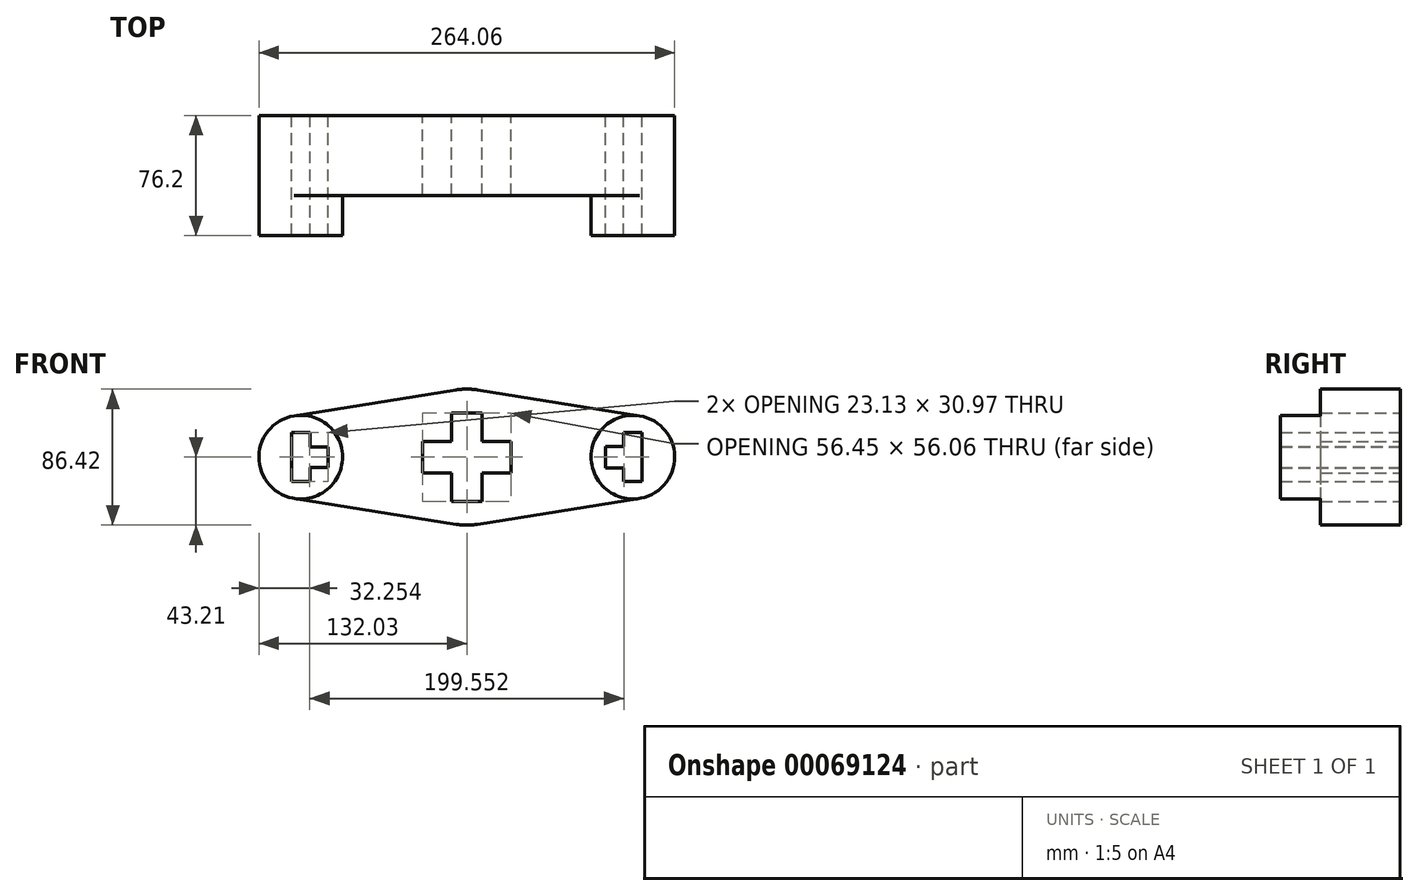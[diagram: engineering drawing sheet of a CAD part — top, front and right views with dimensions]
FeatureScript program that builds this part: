
annotation { "Feature Type Name" : "Feature", "Feature Type Description" : "" }
export const myFeature = defineFeature(function(context is Context, id is Id, definition is map)
    precondition{}
    {
        {
            var Q0;
            Q0=qCreatedBy(makeId("Front.planeOp"),FACE);
            var sketch = newSketch(context, id + "F0", { "sketchPlane" : qUnion([Q0])});
            skCircle(sketch, "E0", {"center": v(0, 0) * mm, "radius": 43.2 * mm});
            skCircle(sketch, "E1", {"center": v(105.46, 0) * mm, "radius": 26.57 * mm});
            skCircle(sketch, "E2", {"center": v(-105.46, 0) * mm, "radius": 26.57 * mm});
            skLineSegment(sketch, "E3", {"start": v(-6.82, 42.66) * mm, "end": v(-109.65, 26.23) * mm});
            skLineSegment(sketch, "E4", {"start": v(-6.82, -42.66) * mm, "end": v(-109.65, -26.23) * mm});
            skLineSegment(sketch, "E5", {"start": v(6.82, 42.66) * mm, "end": v(109.65, 26.23) * mm});
            skLineSegment(sketch, "E6", {"start": v(6.82, -42.66) * mm, "end": v(109.65, -26.23) * mm});
            skLineSegment(sketch, "E7.rect.bottom", {"start": v(-122.71, 6.47) * mm, "end": v(-88.21, 6.47) * mm});
            skLineSegment(sketch, "E7.rect.top", {"start": v(-122.71, -6.47) * mm, "end": v(-88.21, -6.47) * mm});
            skLineSegment(sketch, "E7.rect.left", {"start": v(-122.71, 6.47) * mm, "end": v(-122.71, -6.47) * mm});
            skLineSegment(sketch, "E7.rect.right", {"start": v(-88.21, 6.47) * mm, "end": v(-88.21, -6.47) * mm});
            skLineSegment(sketch, "E8.rect.bottom", {"start": v(-111.34, 15.49) * mm, "end": v(-99.58, 15.49) * mm});
            skLineSegment(sketch, "E8.rect.top", {"start": v(-111.34, -15.49) * mm, "end": v(-99.58, -15.49) * mm});
            skLineSegment(sketch, "E8.rect.left", {"start": v(-111.34, 15.49) * mm, "end": v(-111.34, -15.49) * mm});
            skLineSegment(sketch, "E8.rect.right", {"start": v(-99.58, 15.49) * mm, "end": v(-99.58, -15.49) * mm});
            skLineSegment(sketch, "E9.rect.bottom", {"start": v(-28.23, 10) * mm, "end": v(28.23, 10) * mm});
            skLineSegment(sketch, "E9.rect.top", {"start": v(-28.23, -10) * mm, "end": v(28.23, -10) * mm});
            skLineSegment(sketch, "E9.rect.left", {"start": v(-28.23, 10) * mm, "end": v(-28.23, -10) * mm});
            skLineSegment(sketch, "E9.rect.right", {"start": v(28.23, 10) * mm, "end": v(28.23, -10) * mm});
            skLineSegment(sketch, "E10.rect.bottom", {"start": v(-9.8, 28.03) * mm, "end": v(9.8, 28.03) * mm});
            skLineSegment(sketch, "E10.rect.top", {"start": v(-9.8, -28.03) * mm, "end": v(9.8, -28.03) * mm});
            skLineSegment(sketch, "E10.rect.left", {"start": v(-9.8, 28.03) * mm, "end": v(-9.8, -28.03) * mm});
            skLineSegment(sketch, "E10.rect.right", {"start": v(9.8, 28.03) * mm, "end": v(9.8, -28.03) * mm});
            skLineSegment(sketch, "E11.rect.bottom", {"start": v(88.21, 6.86) * mm, "end": v(122.71, 6.86) * mm});
            skLineSegment(sketch, "E11.rect.top", {"start": v(88.21, -6.86) * mm, "end": v(122.71, -6.86) * mm});
            skLineSegment(sketch, "E11.rect.left", {"start": v(88.21, 6.86) * mm, "end": v(88.21, -6.86) * mm});
            skLineSegment(sketch, "E11.rect.right", {"start": v(122.71, 6.86) * mm, "end": v(122.71, -6.86) * mm});
            skLineSegment(sketch, "E12.rect.bottom", {"start": v(99.58, 15.49) * mm, "end": v(111.34, 15.49) * mm});
            skLineSegment(sketch, "E12.rect.top", {"start": v(99.58, -15.49) * mm, "end": v(111.34, -15.49) * mm});
            skLineSegment(sketch, "E12.rect.left", {"start": v(99.58, 15.49) * mm, "end": v(99.58, -15.49) * mm});
            skLineSegment(sketch, "E12.rect.right", {"start": v(111.34, 15.49) * mm, "end": v(111.34, -15.49) * mm});
            skSolve(sketch);
        }
        {
            var Q0;
            {var subQ0=sQuery(id+"F0.wireOp",EDGE,"E3");Q0=makeQuery(id+"F0.imprint","IMPRINT",FACE,{"disambiguationData":[TD([[makeQuery(id+"F0.imprint","IMPRINT",EDGE,{"derivedFrom":subQ0}),1.0]])]});}
            var Q1;
            {var subQ0=sQuery(id+"F0.wireOp",EDGE,"E5");Q1=makeQuery(id+"F0.imprint","IMPRINT",FACE,{"disambiguationData":[TD([[makeQuery(id+"F0.imprint","IMPRINT",EDGE,{"derivedFrom":subQ0}),-1.0]])]});}
            var Q2;
            {var subQ1=sQuery(id+"F0.wireOp",EDGE,"E11.rect.left");Q2=makeQuery(id+"F0.imprint","IMPRINT",FACE,{"disambiguationData":[TD([[makeQuery(id+"F0.imprint","IMPRINT",EDGE,{"derivedFrom":subQ1}),-1.0]])]});}
            var Q3;
            {var subQ1=sQuery(id+"F0.wireOp",EDGE,"E9.rect.left");Q3=makeQuery(id+"F0.imprint","IMPRINT",FACE,{"disambiguationData":[TD([[makeQuery(id+"F0.imprint","IMPRINT",EDGE,{"derivedFrom":subQ1}),-1.0]])]});}
            var Q4;
            {var subQ6=sQuery(id+"F0.wireOp",EDGE,"E7.rect.left");Q4=makeQuery(id+"F0.imprint","IMPRINT",FACE,{"disambiguationData":[TD([[makeQuery(id+"F0.imprint","IMPRINT",EDGE,{"derivedFrom":subQ6}),-1.0]])]});}
            var Q5;
            {var subQ0=sQuery(id+"F0.wireOp",EDGE,"E7.rect.left");Q5=makeQuery(id+"F0.imprint","IMPRINT",FACE,{"disambiguationData":[TD([[makeQuery(id+"F0.imprint","IMPRINT",EDGE,{"derivedFrom":subQ0}),1.0]])]});}
            var Q6;
            {var subQ0=sQuery(id+"F0.wireOp",EDGE,"E11.rect.right");Q6=makeQuery(id+"F0.imprint","IMPRINT",FACE,{"disambiguationData":[TD([[makeQuery(id+"F0.imprint","IMPRINT",EDGE,{"derivedFrom":subQ0}),-1.0]])]});}
            extrude(context, id + "F1", {"entities" : qUnion([Q0, Q1, Q2, Q3, Q4, Q5, Q6]), "depth" : 25.4 * mm});
        }
        {
            var Q0;
            {var subQ6=sQuery(id+"F0.wireOp",EDGE,"E7.rect.left");Q0=makeQuery(id+"F0.imprint","IMPRINT",FACE,{"disambiguationData":[TD([[makeQuery(id+"F0.imprint","IMPRINT",EDGE,{"derivedFrom":subQ6}),-1.0]])]});}
            var Q1;
            {var subQ1=sQuery(id+"F0.wireOp",EDGE,"E9.rect.left");Q1=makeQuery(id+"F0.imprint","IMPRINT",FACE,{"disambiguationData":[TD([[makeQuery(id+"F0.imprint","IMPRINT",EDGE,{"derivedFrom":subQ1}),-1.0]])]});}
            var Q2;
            {var subQ1=sQuery(id+"F0.wireOp",EDGE,"E11.rect.left");Q2=makeQuery(id+"F0.imprint","IMPRINT",FACE,{"disambiguationData":[TD([[makeQuery(id+"F0.imprint","IMPRINT",EDGE,{"derivedFrom":subQ1}),-1.0]])]});}
            var Q3;
            {var subQ0=sQuery(id+"F0.wireOp",EDGE,"E7.rect.left");Q3=makeQuery(id+"F0.imprint","IMPRINT",FACE,{"disambiguationData":[TD([[makeQuery(id+"F0.imprint","IMPRINT",EDGE,{"derivedFrom":subQ0}),1.0]])]});}
            var Q4;
            {var subQ0=sQuery(id+"F0.wireOp",EDGE,"E11.rect.right");Q4=makeQuery(id+"F0.imprint","IMPRINT",FACE,{"disambiguationData":[TD([[makeQuery(id+"F0.imprint","IMPRINT",EDGE,{"derivedFrom":subQ0}),-1.0]])]});}
            extrude(context, id + "F2", {"entities" : qUnion([Q0, Q1, Q2, Q3, Q4]), "operationType" : NewBodyOperationType.ADD, "depth" : 50.8 * mm});
        }
        {
            var Q0;
            {var subQ0=sQuery(id+"F0.wireOp",EDGE,"E3");var subQ1=sQuery(id+"F0.wireOp",EDGE,"E2");var subQ2=sQuery(id+"F0.wireOp",EDGE,"E4");var subQ3=sQuery(id+"F0.wireOp",EDGE,"E0");var subQ4=sQuery(id+"F0.wireOp",EDGE,"E6");var subQ5=sQuery(id+"F0.wireOp",EDGE,"E5");Q0=makeQuery(id+"F2.boolean.opBoolean","SPLIT",FACE,{"disambiguationData":[TD([makeQuery(id+"F1.opExtrude","SWEPT_FACE",FACE,{"disambiguationData":[OSD([subQ1])]})])],"derivedFrom":makeQuery(id+"F1.opExtrude","CAP_FACE",FACE,{"disambiguationData":[OSD([subQ3,sQuery(id+"F0.wireOp",EDGE,"E1"),subQ1,subQ0,subQ2,subQ5,subQ4,sQuery(id+"F0.wireOp",EDGE,"E7.rect.bottom"),sQuery(id+"F0.wireOp",EDGE,"E7.rect.top"),sQuery(id+"F0.wireOp",EDGE,"E7.rect.left"),sQuery(id+"F0.wireOp",EDGE,"E7.rect.right"),sQuery(id+"F0.wireOp",EDGE,"E8.rect.bottom"),sQuery(id+"F0.wireOp",EDGE,"E8.rect.top"),sQuery(id+"F0.wireOp",EDGE,"E8.rect.left"),sQuery(id+"F0.wireOp",EDGE,"E8.rect.right"),sQuery(id+"F0.wireOp",EDGE,"E9.rect.bottom"),sQuery(id+"F0.wireOp",EDGE,"E9.rect.top"),sQuery(id+"F0.wireOp",EDGE,"E9.rect.left"),sQuery(id+"F0.wireOp",EDGE,"E9.rect.right"),sQuery(id+"F0.wireOp",EDGE,"E10.rect.bottom"),sQuery(id+"F0.wireOp",EDGE,"E10.rect.top"),sQuery(id+"F0.wireOp",EDGE,"E10.rect.left"),sQuery(id+"F0.wireOp",EDGE,"E10.rect.right"),sQuery(id+"F0.wireOp",EDGE,"E11.rect.bottom"),sQuery(id+"F0.wireOp",EDGE,"E11.rect.top"),sQuery(id+"F0.wireOp",EDGE,"E11.rect.left"),sQuery(id+"F0.wireOp",EDGE,"E11.rect.right"),sQuery(id+"F0.wireOp",EDGE,"E12.rect.bottom"),sQuery(id+"F0.wireOp",EDGE,"E12.rect.top"),sQuery(id+"F0.wireOp",EDGE,"E12.rect.left"),sQuery(id+"F0.wireOp",EDGE,"E12.rect.right")])],"isStart":false})});}
            var Q1;
            Q1=makeQuery(id+"F2.opExtrude","CAP_FACE",FACE,{"disambiguationData":[OSD([sQuery(id+"F0.wireOp",EDGE,"E2"),sQuery(id+"F0.wireOp",EDGE,"E7.rect.bottom"),sQuery(id+"F0.wireOp",EDGE,"E7.rect.top"),sQuery(id+"F0.wireOp",EDGE,"E7.rect.left"),sQuery(id+"F0.wireOp",EDGE,"E7.rect.right"),sQuery(id+"F0.wireOp",EDGE,"E8.rect.bottom"),sQuery(id+"F0.wireOp",EDGE,"E8.rect.top"),sQuery(id+"F0.wireOp",EDGE,"E8.rect.left"),sQuery(id+"F0.wireOp",EDGE,"E8.rect.right")])],"isStart":false});
            var Q2;
            {var subQ0=sQuery(id+"F0.wireOp",EDGE,"E1");var subQ1=sQuery(id+"F0.wireOp",EDGE,"E5");var subQ2=sQuery(id+"F0.wireOp",EDGE,"E4");var subQ3=sQuery(id+"F0.wireOp",EDGE,"E0");var subQ4=sQuery(id+"F0.wireOp",EDGE,"E6");var subQ5=sQuery(id+"F0.wireOp",EDGE,"E3");Q2=makeQuery(id+"F2.boolean.opBoolean","SPLIT",FACE,{"disambiguationData":[TD([makeQuery(id+"F1.opExtrude","SWEPT_FACE",FACE,{"disambiguationData":[OSD([subQ0])]})])],"derivedFrom":makeQuery(id+"F1.opExtrude","CAP_FACE",FACE,{"disambiguationData":[OSD([subQ3,subQ0,sQuery(id+"F0.wireOp",EDGE,"E2"),subQ5,subQ2,subQ1,subQ4,sQuery(id+"F0.wireOp",EDGE,"E7.rect.bottom"),sQuery(id+"F0.wireOp",EDGE,"E7.rect.top"),sQuery(id+"F0.wireOp",EDGE,"E7.rect.left"),sQuery(id+"F0.wireOp",EDGE,"E7.rect.right"),sQuery(id+"F0.wireOp",EDGE,"E8.rect.bottom"),sQuery(id+"F0.wireOp",EDGE,"E8.rect.top"),sQuery(id+"F0.wireOp",EDGE,"E8.rect.left"),sQuery(id+"F0.wireOp",EDGE,"E8.rect.right"),sQuery(id+"F0.wireOp",EDGE,"E9.rect.bottom"),sQuery(id+"F0.wireOp",EDGE,"E9.rect.top"),sQuery(id+"F0.wireOp",EDGE,"E9.rect.left"),sQuery(id+"F0.wireOp",EDGE,"E9.rect.right"),sQuery(id+"F0.wireOp",EDGE,"E10.rect.bottom"),sQuery(id+"F0.wireOp",EDGE,"E10.rect.top"),sQuery(id+"F0.wireOp",EDGE,"E10.rect.left"),sQuery(id+"F0.wireOp",EDGE,"E10.rect.right"),sQuery(id+"F0.wireOp",EDGE,"E11.rect.bottom"),sQuery(id+"F0.wireOp",EDGE,"E11.rect.top"),sQuery(id+"F0.wireOp",EDGE,"E11.rect.left"),sQuery(id+"F0.wireOp",EDGE,"E11.rect.right"),sQuery(id+"F0.wireOp",EDGE,"E12.rect.bottom"),sQuery(id+"F0.wireOp",EDGE,"E12.rect.top"),sQuery(id+"F0.wireOp",EDGE,"E12.rect.left"),sQuery(id+"F0.wireOp",EDGE,"E12.rect.right")])],"isStart":false})});}
            var Q3;
            Q3=makeQuery(id+"F2.opExtrude","CAP_FACE",FACE,{"disambiguationData":[OSD([sQuery(id+"F0.wireOp",EDGE,"E1"),sQuery(id+"F0.wireOp",EDGE,"E11.rect.bottom"),sQuery(id+"F0.wireOp",EDGE,"E11.rect.top"),sQuery(id+"F0.wireOp",EDGE,"E11.rect.left"),sQuery(id+"F0.wireOp",EDGE,"E11.rect.right"),sQuery(id+"F0.wireOp",EDGE,"E12.rect.bottom"),sQuery(id+"F0.wireOp",EDGE,"E12.rect.top"),sQuery(id+"F0.wireOp",EDGE,"E12.rect.left"),sQuery(id+"F0.wireOp",EDGE,"E12.rect.right")])],"isStart":false});
            extrude(context, id + "F3", {"entities" : qUnion([Q0, Q1, Q2, Q3]), "operationType" : NewBodyOperationType.ADD, "depth" : 25.4 * mm});
        }
    });
